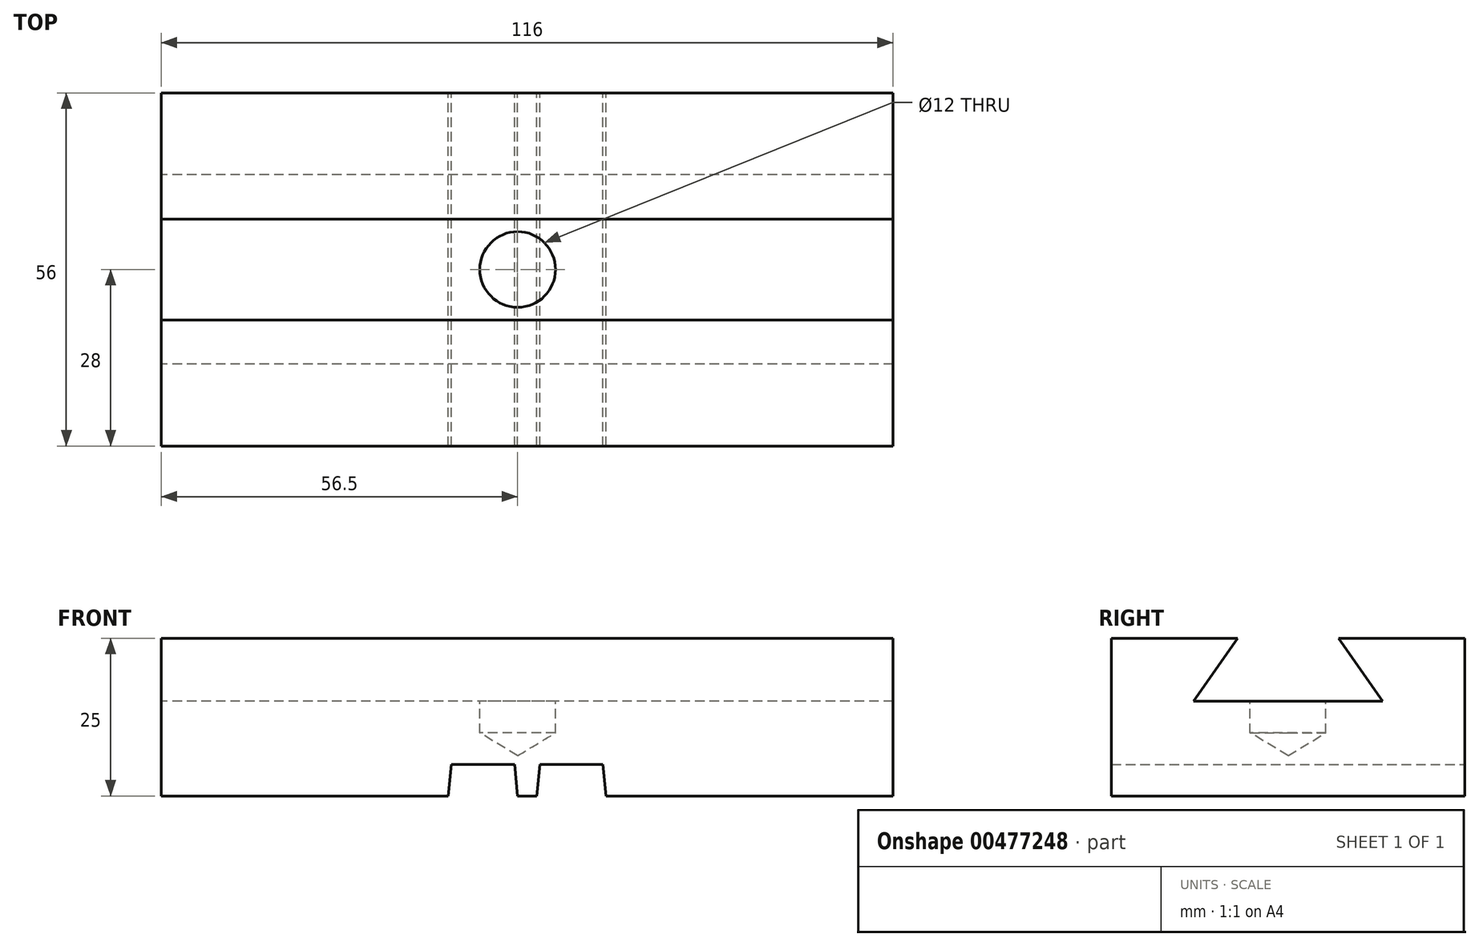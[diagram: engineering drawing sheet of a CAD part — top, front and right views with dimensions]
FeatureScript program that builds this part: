
annotation { "Feature Type Name" : "Feature", "Feature Type Description" : "" }
export const myFeature = defineFeature(function(context is Context, id is Id, definition is map)
    precondition{}
    {
        {
            var Q0;
            Q0=qCreatedBy(makeId("Front.planeOp"),FACE);
            var sketch = newSketch(context, id + "F0", { "sketchPlane" : qUnion([Q0])});
            skLineSegment(sketch, "E0", {"start": v(0, 0) * mm, "end": v(1.5, 0) * mm});
            skLineSegment(sketch, "E1", {"start": v(1.5, 0) * mm, "end": v(2, 5) * mm});
            skLineSegment(sketch, "E2", {"start": v(2, 5) * mm, "end": v(12, 5) * mm});
            skLineSegment(sketch, "E3", {"start": v(12, 5) * mm, "end": v(12.5, 0) * mm});
            skLineSegment(sketch, "E4", {"start": v(12.5, 0) * mm, "end": v(58, 0) * mm});
            skLineSegment(sketch, "E5", {"start": v(58, 0) * mm, "end": v(58, 25) * mm});
            skLineSegment(sketch, "E6", {"start": v(-58, 25) * mm, "end": v(-58, 0) * mm});
            skLineSegment(sketch, "E7", {"start": v(-58, 0) * mm, "end": v(-12.5, 0) * mm});
            skLineSegment(sketch, "E8", {"start": v(-12.5, 0) * mm, "end": v(-12, 5) * mm});
            skLineSegment(sketch, "E9", {"start": v(-12, 5) * mm, "end": v(-2, 5) * mm});
            skLineSegment(sketch, "E10", {"start": v(-2, 5) * mm, "end": v(-1.5, 0) * mm});
            skLineSegment(sketch, "E11", {"start": v(-1.5, 0) * mm, "end": v(0, 0) * mm});
            skLineSegment(sketch, "E12", {"start": v(-58, 25) * mm, "end": v(58, 25) * mm});
            skSolve(sketch);
        }
        {
            var Q0;
            Q0=makeQuery(id+"F0.imprint","IMPRINT",FACE,{"disambiguationData":[TD([[makeQuery(id+"F0.imprint","IMPRINT",EDGE,{"derivedFrom":sQuery(id+"F0.wireOp",EDGE,"E0")}),1.0]])]});
            extrude(context, id + "F1", {"entities" : qUnion([Q0]), "depth" : 56 * mm});
        }
        {
            var Q0;
            Q0=makeQuery(id+"F1.opExtrude","SWEPT_FACE",FACE,{"disambiguationData":[OSD([sQuery(id+"F0.wireOp",EDGE,"E6")])]});
            var sketch = newSketch(context, id + "F2", { "sketchPlane" : qUnion([Q0])});
            skLineSegment(sketch, "E13", {"start": v(0, 25) * mm, "end": v(28, 25) * mm});
            skLineSegment(sketch, "E14", {"start": v(28, 25) * mm, "end": v(28, 15) * mm});
            skLineSegment(sketch, "E15", {"start": v(28, 15) * mm, "end": v(43, 15) * mm});
            skLineSegment(sketch, "E16", {"start": v(43, 15) * mm, "end": v(36, 25) * mm});
            skLineSegment(sketch, "E17", {"start": v(28, 15) * mm, "end": v(13, 15) * mm});
            skLineSegment(sketch, "E18", {"start": v(13, 15) * mm, "end": v(20, 25) * mm});
            skLineSegment(sketch, "E19", {"start": v(36, 25) * mm, "end": v(20, 25) * mm});
            skSolve(sketch);
        }
        {
            var Q0;
            {var subQ0=sQuery(id+"F2.wireOp",EDGE,"E14");Q0=makeQuery(id+"F2.imprint","IMPRINT",FACE,{"disambiguationData":[TD([[makeQuery(id+"F2.imprint","IMPRINT",EDGE,{"derivedFrom":subQ0}),-1.0]])]});}
            var Q1;
            {var subQ0=sQuery(id+"F2.wireOp",EDGE,"E14");Q1=makeQuery(id+"F2.imprint","IMPRINT",FACE,{"disambiguationData":[TD([[makeQuery(id+"F2.imprint","IMPRINT",EDGE,{"derivedFrom":subQ0}),1.0]])]});}
            extrude(context, id + "F3", {"entities" : qUnion([Q0, Q1]), "operationType" : NewBodyOperationType.REMOVE, "endBound" : BoundingType.UP_TO_NEXT, "oppositeDirection" : true, "depth" : 25 * mm});
        }
        {
            var Q0;
            Q0=makeQuery(id+"F3.boolean.opBoolean","COPY",FACE,{"derivedFrom":makeQuery(id+"F3.opExtrude","SWEPT_FACE",FACE,{"disambiguationData":[OSD([sQuery(id+"F2.wireOp",EDGE,"E15"),sQuery(id+"F2.wireOp",EDGE,"E17")])]})});
            var sketch = newSketch(context, id + "F4", { "sketchPlane" : qUnion([Q0])});
            skPoint(sketch, "E20", {"position": v(-1.5, -28) * mm});
            skPoint(sketch, "E20.positionSnap0", {"position": v(0, -13) * mm});
            skSolve(sketch);
        }
        {
            var Q0;
            Q0=sQuery(id+"F4.wireOp",VERTEX,"E20");
            var Q1;
            Q1=makeQuery(id+"F1.opExtrude","SWEPT_BODY",BODY,{"disambiguationData":[OSD([sQuery(id+"F0.wireOp",EDGE,"E0"),sQuery(id+"F0.wireOp",EDGE,"E1"),sQuery(id+"F0.wireOp",EDGE,"E2"),sQuery(id+"F0.wireOp",EDGE,"E3"),sQuery(id+"F0.wireOp",EDGE,"E4"),sQuery(id+"F0.wireOp",EDGE,"E5"),sQuery(id+"F0.wireOp",EDGE,"E6"),sQuery(id+"F0.wireOp",EDGE,"E7"),sQuery(id+"F0.wireOp",EDGE,"E8"),sQuery(id+"F0.wireOp",EDGE,"E9"),sQuery(id+"F0.wireOp",EDGE,"E10"),sQuery(id+"F0.wireOp",EDGE,"E11"),sQuery(id+"F0.wireOp",EDGE,"E12")])]});
            hole(context, id + "F5", {"style" : HoleStyle.SIMPLE, "endStyle" : HoleEndStyle.BLIND, "holeDiameter" : 12 * mm, "holeDepth" : 5 * mm, "isTappedThrough" : true, "tappedDepth" : 12 * mm, "tapClearance" : 3, "locations" : qUnion([Q0]), "scope" : qUnion([Q1])});
        }
    });
